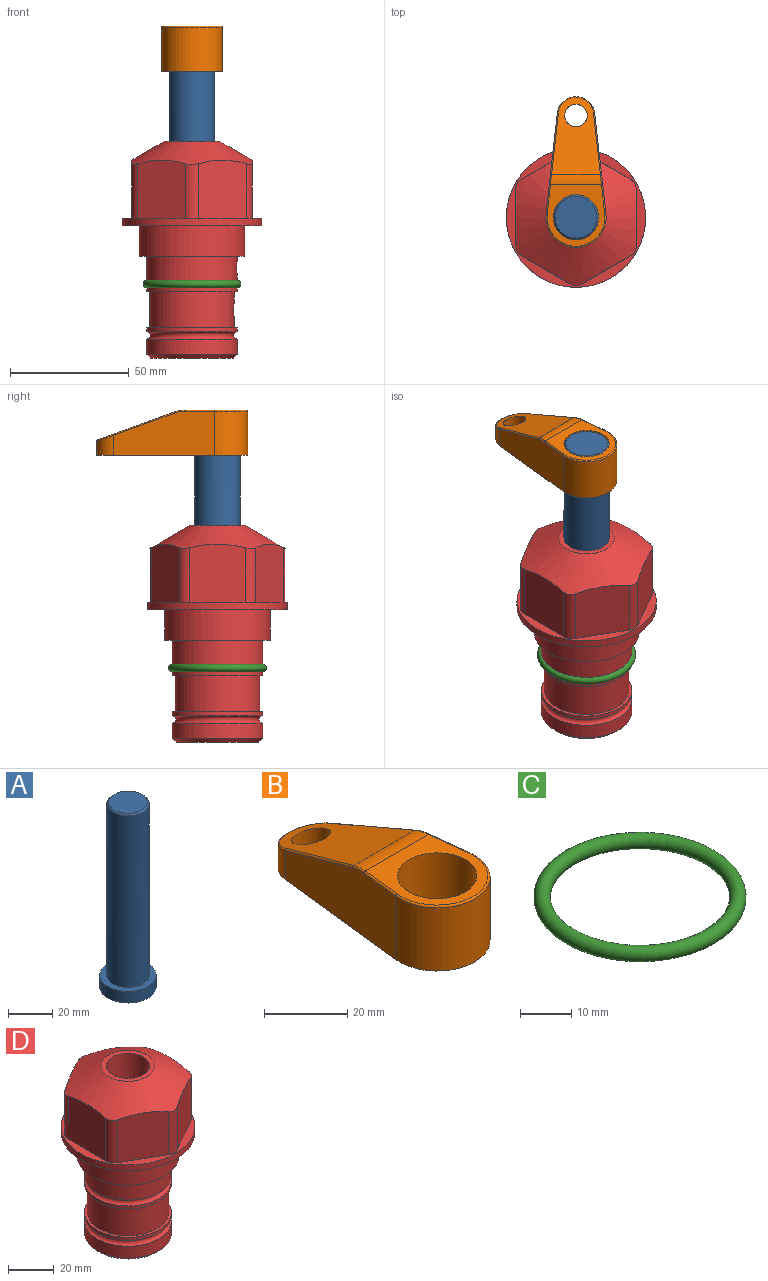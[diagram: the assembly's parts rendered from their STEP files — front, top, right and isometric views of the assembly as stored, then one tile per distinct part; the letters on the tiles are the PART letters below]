
ASSEMBLY  parts=4 mates=2
PART A: 6 faces, bbox 25.4x25.4x101.6 mm
  f0: plane 17.46x17.46mm, normal (0,0,1), area 239.5mm2, adj f5
  f1: plane 25.4x25.4mm, normal (0,0,-1), area 506.7mm2, adj f2
  f2: cylinder r=12.7mm len=25.4mm, axis (0,0,1), area 506.7mm2, adj f1,f3
  f3: plane 25.4x25.4mm, normal (0,0,1), area 221.7mm2, adj f2,f4
  f4: cylinder r=9.53mm len=94.46mm, axis (0,0,1), area 5653mm2, adj f3,f5
  f5: cone r=8.73mm half-angle=45deg, axis (0,0,-1), area 64.4mm2, adj f0,f4
PART B: 44 faces, bbox 27.5x64.5x19.1 mm
  f0: plane 2.3x0.95mm, normal (0,0,-1), area 1mm2, adj f25,f30,f34
  f1: plane 63.5x25.4mm, normal (0,0,-1), area 561.7mm2, adj f2,f3,f4,f5,f6,f7,f19,f20
  f2: cylinder r=12.7mm len=25.4mm, axis (0,0,-1), area 792.2mm2, adj f1,f3,f5,f13
  f3: plane 42.33x18.54mm, normal (0.99,0.11,0), area 647mm2, adj f1,f2,f4,f11,f12,f14
  f4: cylinder r=7.94mm len=15.78mm, axis (0,0,-1), area 158.6mm2, adj f1,f3,f5,f16
  f5: plane 42.33x18.54mm, normal (-0.99,0.11,0), area 647mm2, adj f1,f2,f4,f15,f17,f18
  f6: cylinder r=9.53mm len=19.05mm, axis (0,0,-1), area 1140.1mm2, adj f1,f8
  f7: cylinder r=4.76mm len=10.98mm, axis (0,0,-1), area 276.1mm2, adj f1,f9
  f8: plane 25.83x24.38mm, normal (0,0,1), area 262.2mm2, adj f6,f10,f11,f13,f15
  f9: plane 32.49x20.55mm, normal (0,0.34,0.94), area 489.9mm2, adj f7,f10,f14,f16,f18
  f10: cylinder r=12.7mm len=21.49mm, axis (-1,0,0), area 93.2mm2, adj f8,f9,f12,f17
  f11: cylinder r=0.51mm len=12.34mm, axis (0.11,-0.99,0), area 9.9mm2, adj f3,f8,f12,f13
  f12: bspline ~7.62x1.64mm, area 3.5mm2, adj f3,f10,f11,f14
  f13: torus R=12.19mm, axis (0,0,1), area 33.6mm2, adj f2,f8,f11,f15
  f14: cylinder r=0.51mm len=26.01mm, axis (0.1,-0.93,0.34), area 21.6mm2, adj f3,f9,f12,f16
  f15: cylinder r=0.51mm len=12.34mm, axis (0.11,0.99,0), area 9.9mm2, adj f5,f8,f13,f17
  f16: bspline ~15.78x7.05mm, area 15.7mm2, adj f4,f9,f14,f18
  f17: bspline ~7.62x1.64mm, area 3.5mm2, adj f5,f10,f15,f18
  f18: cylinder r=0.51mm len=26.01mm, axis (0.1,0.93,-0.34), area 21.6mm2, adj f5,f9,f16,f17
  f19: plane 21.6x14.29mm, normal (-0.99,-0.11,0), area 242.6mm2, adj f1,f26,f28,f34,f36,f38
  f20: plane 21.6x14.29mm, normal (0.99,-0.11,0), area 242.6mm2, adj f1,f27,f29,f37,f39,f41
  f21: cylinder r=12.7mm len=14.29mm, axis (0,0,-1), area 173.2mm2, adj f1,f26,f27,f30,f31,f33
  f22: cylinder r=7.94mm len=7.63mm, axis (0,0,-1), area 53.8mm2, adj f1,f28,f29,f42
  f23: plane 2.3x0.95mm, normal (0,0,-1), area 1mm2, adj f25,f33,f37
  f24: plane 17.94x12.32mm, normal (0,-0.34,-0.94), area 191.2mm2, adj f25,f38,f41,f42
  f25: cylinder r=9.53mm len=12.93mm, axis (-1,0,0), area 37.5mm2, adj f0,f23,f24,f31,f36,f39
  f26: cylinder r=1.59mm len=14.29mm, axis (0,0,-1), area 49mm2, adj f1,f19,f21,f32
  f27: cylinder r=1.59mm len=14.29mm, axis (0,0,-1), area 49mm2, adj f1,f20,f21,f35
  f28: cylinder r=1.59mm len=7.28mm, axis (0,0,-1), area 22.1mm2, adj f1,f19,f22,f40
  f29: cylinder r=1.59mm len=7.28mm, axis (0,0,-1), area 22.1mm2, adj f1,f20,f22,f43
  f30: torus R=14.29mm, axis (0,0,1), area 5.8mm2, adj f0,f21,f31,f32
  f31: bspline ~11.06x2.73mm, area 20.8mm2, adj f21,f25,f30,f33
  f32: sphere r=1.59mm, area 5.4mm2, adj f26,f30,f34
  f33: torus R=14.29mm, axis (0,0,1), area 5.8mm2, adj f21,f23,f31,f35
  f34: cylinder r=1.59mm len=1.68mm, axis (-0.11,0.99,0), area 2.4mm2, adj f0,f19,f32,f36
  f35: sphere r=1.59mm, area 5.4mm2, adj f27,f33,f37
  f36: bspline ~5.82x2.33mm, area 7.7mm2, adj f19,f25,f34,f38
  f37: cylinder r=1.59mm len=1.68mm, axis (0.11,0.99,0), area 2.4mm2, adj f20,f23,f35,f39
  f38: cylinder r=1.59mm len=18.33mm, axis (0.1,-0.93,0.34), area 46.7mm2, adj f19,f24,f36,f40
  f39: bspline ~5.82x2.33mm, area 7.7mm2, adj f20,f25,f37,f41
  f40: sphere r=1.59mm, area 3.6mm2, adj f28,f38,f42
  f41: cylinder r=1.59mm len=18.33mm, axis (0.1,0.93,-0.34), area 46.7mm2, adj f20,f24,f39,f43
  f42: bspline ~8.31x1.84mm, area 15.3mm2, adj f22,f24,f40,f43
  f43: sphere r=1.59mm, area 3.6mm2, adj f29,f41,f42
PART C: 1 faces, bbox 44.7x44.7x3.2 mm
  f0: torus R=19.05mm, axis (0,0,1), area 1193.9mm2
PART D: 36 faces, bbox 58.7x58.7x91.2 mm
  f0: cylinder r=17.78mm len=35.56mm, axis (0,0,1), area 1670.8mm2, adj f23,f24,f31
  f1: cylinder r=19.05mm len=38.1mm, axis (0,0,1), area 1191.9mm2, adj f26,f27,f30
  f2: plane 58.66x58.66mm, normal (0,0,-1), area 1150.6mm2, adj f3,f28
  f3: cylinder r=29.33mm len=58.66mm, axis (0,0,-1), area 585.1mm2, adj f2,f4
  f4: plane 58.66x58.66mm, normal (0,0,1), area 475.9mm2, adj f3,f5,f6,f7,f8,f9,f10,f11
  f5: plane 24.5x20.32mm, normal (-0.5,0.87,0), area 562.8mm2, adj f4,f15,f16,f17
  f6: plane 24.5x20.32mm, normal (0.5,0.87,0), area 562.8mm2, adj f4,f14,f15,f17
  f7: plane 24.5x23.48mm, normal (1,0,0), area 562.8mm2, adj f4,f13,f14,f17
  f8: plane 24.5x20.32mm, normal (0.5,-0.87,0), area 562.8mm2, adj f4,f12,f13,f17
  f9: plane 24.5x20.32mm, normal (-0.5,-0.87,0), area 562.8mm2, adj f4,f11,f12,f17
  f10: plane 24.5x23.48mm, normal (-1,0,0), area 562.8mm2, adj f4,f11,f16,f17
  f11: cylinder r=5.08mm len=23.01mm, axis (0,0,-1), area 121.2mm2, adj f4,f9,f10,f17
  f12: cylinder r=5.08mm len=23.01mm, axis (0,0,-1), area 121.2mm2, adj f4,f8,f9,f17
  f13: cylinder r=5.08mm len=23.01mm, axis (0,0,-1), area 121.2mm2, adj f4,f7,f8,f17
  f14: cylinder r=5.08mm len=23.01mm, axis (0,0,-1), area 121.2mm2, adj f4,f6,f7,f17
  f15: cylinder r=5.08mm len=23.01mm, axis (0,0,-1), area 121.2mm2, adj f4,f5,f6,f17
  f16: cylinder r=5.08mm len=23.01mm, axis (0,0,-1), area 121.2mm2, adj f4,f5,f10,f17
  f17: cone r=11.73mm half-angle=60deg, axis (0,0,-1), area 2071.8mm2, adj f5,f6,f7,f8,f9,f10,f11,f12
  f18: plane 23.46x23.46mm, normal (0,0,1), area 147.4mm2, adj f17,f35
  f19: plane 34.93x34.93mm, normal (0,0,-1), area 958mm2, adj f29
  f20: cylinder r=19.05mm len=38.1mm, axis (0,0,1), area 760.1mm2, adj f21,f29
  f21: torus R=19.05mm, axis (0,0,1), area 565.3mm2, adj f20,f22
  f22: cylinder r=19.05mm len=38.1mm, axis (0,0,1), area 190mm2, adj f21,f23
  f23: plane 38.1x38.1mm, normal (0,0,1), area 146.9mm2, adj f0,f22
  f24: plane 38.1x38.1mm, normal (0,0,-1), area 146.9mm2, adj f0,f25
  f25: cylinder r=19.05mm len=38.1mm, axis (0,0,1), area 190mm2, adj f24,f26
  f26: torus R=19.05mm, axis (0,0,1), area 565.3mm2, adj f1,f25
  f27: plane 44.45x44.45mm, normal (0,0,-1), area 411.7mm2, adj f1,f28
  f28: cylinder r=22.23mm len=44.45mm, axis (0,0,1), area 1773.5mm2, adj f2,f27
  f29: cone r=19.05mm half-angle=45deg, axis (0,0,1), area 257.5mm2, adj f19,f20
  f30: cylinder r=3.17mm len=6.75mm, axis (-1,0,0), area 128mm2, adj f1,f33
  f31: cylinder r=3.17mm len=6.35mm, axis (-1,0,0), area 102.5mm2, adj f0,f33
  f32: plane 25.4x25.4mm, normal (0,0,1), area 506.7mm2, adj f33
  f33: cylinder r=12.7mm len=66.42mm, axis (0,0,-1), area 5236.2mm2, adj f30,f31,f32,f34
  f34: cone r=9.53mm half-angle=30deg, axis (0,0,-1), area 443.4mm2, adj f33,f35
  f35: cylinder r=9.53mm len=19.05mm, axis (0,0,-1), area 849mm2, adj f18,f34
PLACE A t=(0,0,10.52)mm
PLACE B t=(0,0,65.13)mm
PLACE C at identity
PLACE D at identity fixed
MATE cylindrical A.f2 <-> D.f0  axis (0,0,1) through (0,0,36.16)mm
MATE fastened B.f2 <-> A.f2  axis (0,0,-1) through (0,0,84.18)mm
